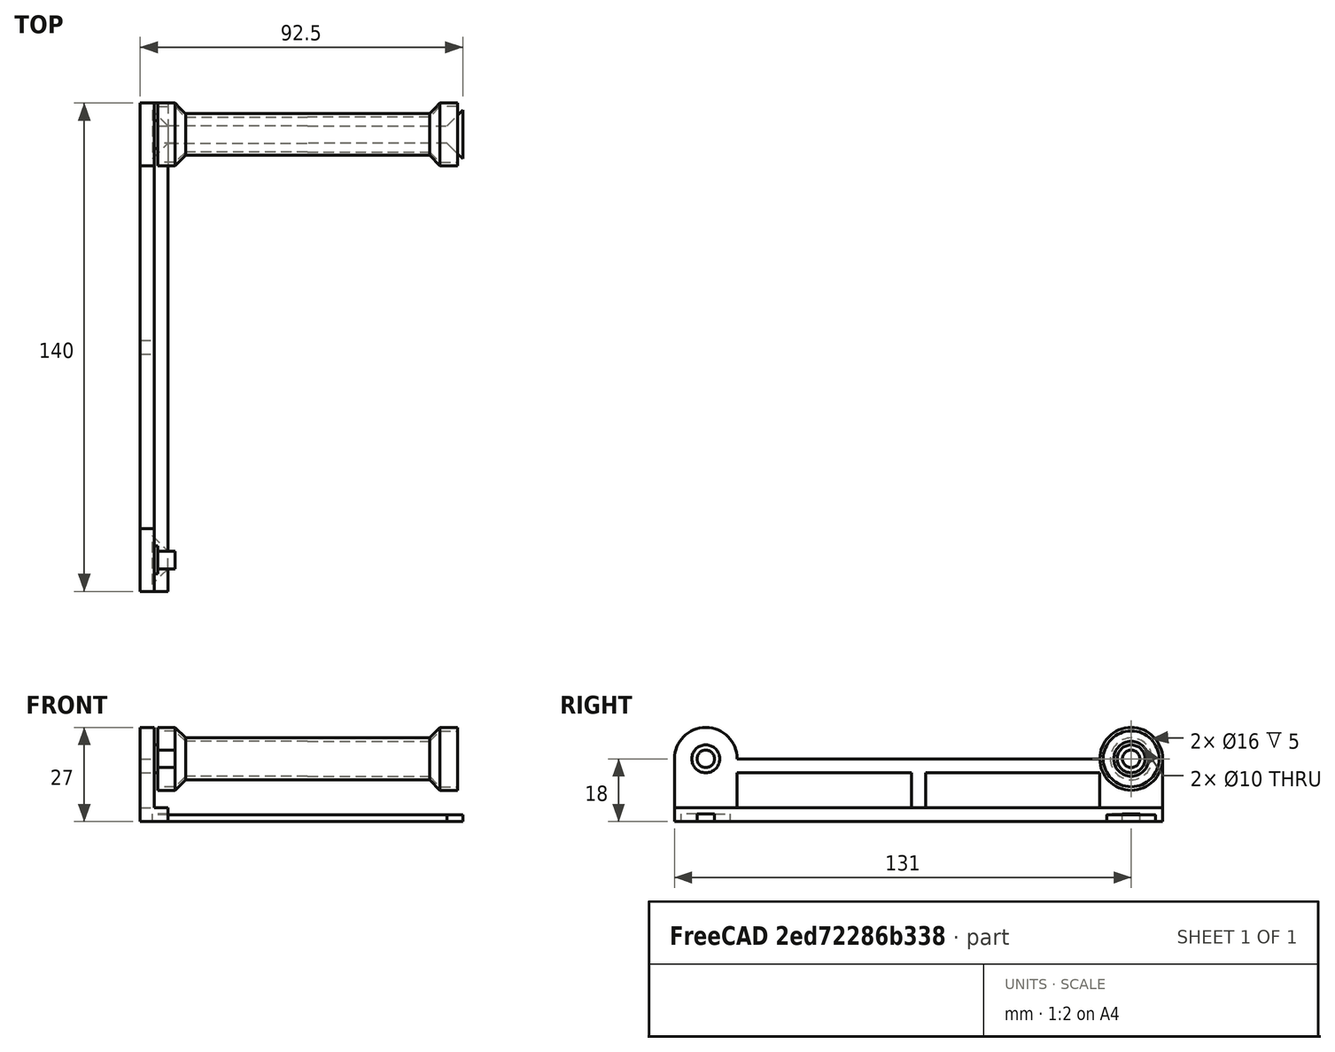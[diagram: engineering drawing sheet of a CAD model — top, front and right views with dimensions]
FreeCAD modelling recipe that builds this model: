
FCSTD DOCUMENT  (FreeCAD 0.21R33771 (Git))
Label: FilamentRoller
License: All rights reserved
LicenseURL: http://en.wikipedia.org/wiki/All_rights_reserved
objects: Sketcher::SketchObject×7, PartDesign::Pad×7, PartDesign::Mirrored×3, PartDesign::Body×3, Mesh::Feature×3, PartDesign::AdditiveLoft×1, PartDesign::SubShapeBinder×1, PartDesign::Pocket×1
note: 32 computed .brp shape members not serialized (recipe doc carries the construction recipe); baked Part::Feature solids carry a one-line shape summary decoded from their .brp

FEATURE [Sketcher::SketchObject] Sketch  label="FloorSketch"
  FullyConstrained = true
  MapMode = 5
  Support = -> [XY_Plane]
  sketch-geometry (4):
    g0: LineSegment StartX=-48 StartY=70 StartZ=0 EndX=-40 EndY=70 EndZ=0
    g1: LineSegment StartX=-40 StartY=70 StartZ=0 EndX=-40 EndY=0 EndZ=0
    g2: LineSegment StartX=-40 StartY=0 StartZ=0 EndX=-48 EndY=0 EndZ=0
    g3: LineSegment StartX=-48 StartY=0 StartZ=0 EndX=-48 EndY=70 EndZ=0
  constraints (12):
    c: Coincident(g0,g1)
    c: Coincident(g1,g2)
    c: Coincident(g2,g3)
    c: Coincident(g3,g0)
    c: Horizontal(g0)
    c: Horizontal(g2)
    c: Vertical(g1)
    c: DistanceX(g0,g0) = 8
    c: DistanceX(g0,g-1) = 48
    c: DistanceY(g-1,g0) = 70
    c: PointOnObject(g2,g-1)
    c: Vertical(g3)
FEATURE [PartDesign::Pad] Pad  label="FloorPad"
  Direction = (0,0,1)
  Length = 4
  Length2 = 10
  Profile = -> Sketch
  ReferenceAxis = -> Sketch [N_Axis]
  Type = 0
FEATURE [Sketcher::SketchObject] Sketch001  label="BearingBackingSketch"
  ExternalGeometry = -> [Pad]
  FullyConstrained = true
  MapMode = 5
  Placement = pos=(-48,0,0) rot=(0.57735,-0.57735,-0.57735;2.0944rad)
  Support = -> [Pad]
  sketch-geometry (12):
    g0: ArcOfCircle CenterX=-61 CenterY=18 CenterZ=0 NormalX=0 NormalY=0 NormalZ=1 AngleXU=0 Radius=9 StartAngle=0 EndAngle=3.14159
    g1: GeomPoint X=-70 Y=18 Z=0
    g2: LineSegment StartX=-70 StartY=4 StartZ=0 EndX=-70 EndY=18 EndZ=0
    g3: LineSegment StartX=-70 StartY=4 StartZ=0 EndX=-52 EndY=4 EndZ=0
    g4: LineSegment StartX=-52 StartY=14 StartZ=0 EndX=-52 EndY=4 EndZ=0
    g5: GeomPoint X=0 Y=18 Z=0
    g6: GeomPoint X=0 Y=4 Z=0
    g7: LineSegment StartX=-52 StartY=18 StartZ=0 EndX=0 EndY=18 EndZ=0
    g8: LineSegment StartX=0 StartY=18 StartZ=0 EndX=0 EndY=4 EndZ=0
    g9: LineSegment StartX=0 StartY=4 StartZ=0 EndX=-2 EndY=4 EndZ=0
    g10: LineSegment StartX=-2 StartY=4 StartZ=0 EndX=-2 EndY=14 EndZ=0
    g11: LineSegment StartX=-2 StartY=14 StartZ=0 EndX=-52 EndY=14 EndZ=0
  constraints (30):
    c: Diameter(g0) = 18  'bearingDiameter'
    c: Vertical(g1,g-5)
    c: Coincident(g2,g-6)
    c: Coincident(g2,g1)
    c: PointOnObject(g4,g-6)
    c: Coincident(g0,g2)
    c: Coincident(g3,g2)
    c: Coincident(g3,g4)
    c: Vertical(g4)
    c: PointOnObject(g5,g-2)
    c: PointOnObject(g6,g-2)
    c: Coincident(g7,g0)
    c: Coincident(g7,g5)
    c: Coincident(g9,g6)
    c: Coincident(g11,g4)
    c: Horizontal(g7)
    c: Vertical(g4,g0)
    c: DistanceY(g4,g0) = 4
    c: Coincident(g8,g7)
    c: Coincident(g8,g9)
    c: Coincident(g9,g10)
    c: Coincident(g10,g11)
    c: PointOnObject(g9,g-6)
    c: PointOnObject(g8,g-6)
    c: Vertical(g10)
    c: DistanceX(g10,g7) = 2
    c: Horizontal(g11)
    c: Horizontal(g0,g0)
    c: Horizontal(g0,g0)
    c: DistanceY(g0) = 18
FEATURE [PartDesign::Pad] Pad001  label="BearingBackingPad"
  BaseFeature = -> Pad
  Direction = (-1,0,0)
  Length = 4
  Length2 = 10
  Profile = -> Sketch001
  ReferenceAxis = -> Sketch001 [N_Axis]
  Reversed = true
  Type = 0
FEATURE [Sketcher::SketchObject] Sketch002  label="BearingPinSketch"
  ExternalGeometry = -> [Pad001]
  FullyConstrained = true
  MapMode = 5
  Placement = pos=(-44,0,0) rot=(0.57735,0.57735,0.57735;2.0944rad)
  Support = -> [Pad001]
  sketch-geometry (1):
    g0: Circle CenterX=61 CenterY=18 CenterZ=0 NormalX=0 NormalY=0 NormalZ=1 AngleXU=0 Radius=2.5
  constraints (2):
    c: Diameter(g0) = 5
    c: Coincident(g0,g-3)
FEATURE [PartDesign::Pad] Pad002  label="BearingPinPad"
  BaseFeature = -> Pad001
  Direction = (1,0,0)
  Length = 6
  Length2 = 10
  Profile = -> Sketch002
  ReferenceAxis = -> Sketch002 [N_Axis]
  Type = 0
FEATURE [Sketcher::SketchObject] Sketch003
  AttachmentOffset = pos=(0,0,-43) rot=(0,0,1;0rad)
  FullyConstrained = true
  MapMode = 5
  Placement = pos=(-43,9.5e-15,-9.5e-15) rot=(0.57735,0.57735,0.57735;2.0944rad)
  Support = -> [YZ_Plane001]
  sketch-geometry (2):
    g0: Circle CenterX=61 CenterY=18 CenterZ=0 NormalX=0 NormalY=0 NormalZ=1 AngleXU=0 Radius=8
    g1: Circle CenterX=61 CenterY=18 CenterZ=0 NormalX=0 NormalY=0 NormalZ=1 AngleXU=0 Radius=9
  constraints (5):
    c: Diameter(g0) = 16
    c: Coincident(g1,g0)
    c: Diameter(g1) = 18
    c: DistanceY(g-1,g0) = 18
    c: DistanceX(g-1,g0) = 61
FEATURE [PartDesign::Pad] Pad003
  Direction = (1,-2e-16,3e-16)
  Length = 5
  Length2 = 10
  Placement = pos=(0,0,0) rot=(0.57735,0.57735,0.57735;2.0944rad)
  Profile = -> Sketch003
  ReferenceAxis = -> Sketch003 [N_Axis]
  Type = 0
FEATURE [Sketcher::SketchObject] Sketch004
  AttachmentOffset = pos=(0,0,-35) rot=(0,0,1;0rad)
  ExternalGeometry = -> [Pad003]
  FullyConstrained = true
  MapMode = 5
  Placement = pos=(-35,7.8e-15,-7.8e-15) rot=(0.57735,0.57735,0.57735;2.0944rad)
  Support = -> [YZ_Plane001]
  sketch-geometry (2):
    g0: Circle CenterX=61 CenterY=18 CenterZ=0 NormalX=0 NormalY=0 NormalZ=1 AngleXU=0 Radius=6
    g1: Circle CenterX=61 CenterY=18 CenterZ=0 NormalX=0 NormalY=0 NormalZ=1 AngleXU=0 Radius=5
  constraints (4):
    c: Coincident(g0,g-3)
    c: Coincident(g1,g0)
    c: Diameter(g0) = 12
    c: Diameter(g1) = 10
FEATURE [PartDesign::AdditiveLoft] AdditiveLoft
  BaseFeature = -> Pad003
  Closed = false
  Placement = pos=(0,0,0) rot=(0.57735,0.57735,0.57735;2.0944rad)
  Profile = -> Pad003 [Face4]
  Ruled = false
  Sections = -> [Sketch004]
FEATURE [PartDesign::Pad] Pad004
  BaseFeature = -> AdditiveLoft
  Direction = (1,-4e-16,8e-16)
  Length = 35
  Length2 = 10
  Placement = pos=(0,0,0) rot=(0.57735,0.57735,0.57735;2.0944rad)
  Profile = -> AdditiveLoft [Face5]
  Type = 0
FEATURE [PartDesign::Mirrored] Mirrored001
  BaseFeature = -> Pad004
  MirrorPlane = -> YZ_Plane001
  Originals = -> [Pad003,AdditiveLoft,Pad004]
  Placement = pos=(0,0,0) rot=(0.57735,0.57735,0.57735;2.0944rad)
FEATURE [PartDesign::Body] Body001  label="Roller"
  Group = -> [Sketch003,Pad003,Sketch004,AdditiveLoft,Pad004,Mirrored001]
  Origin = -> Origin001
  Tip = -> Mirrored001
FEATURE [Sketcher::SketchObject] Sketch005  label="BearingStandoffSketch"
  ExternalGeometry = -> [Pad002]
  FullyConstrained = true
  MapMode = 5
  Placement = pos=(-44,0,0) rot=(0.57735,0.57735,0.57735;2.0944rad)
  Support = -> [Pad002]
  sketch-geometry (1):
    g0: Circle CenterX=61 CenterY=18 CenterZ=0 NormalX=0 NormalY=0 NormalZ=1 AngleXU=0 Radius=4
  constraints (2):
    c: Diameter(g0) = 8
    c: Coincident(g0,g-3)
FEATURE [PartDesign::Pad] Pad005  label="BearingStandoffPadding"
  BaseFeature = -> Pad002
  Direction = (1,0,0)
  Length = 1
  Length2 = 10
  Profile = -> Sketch005
  ReferenceAxis = -> Sketch005 [N_Axis]
  Type = 0
FEATURE [Sketcher::SketchObject] Sketch007  label="BinderBaseSketch"
  FullyConstrained = true
  MapMode = 5
  Support = -> [XY_Plane002]
  sketch-geometry (6):
    g0: LineSegment StartX=-44.5 StartY=68 StartZ=0 EndX=-44.5 EndY=54 EndZ=0
    g1: LineSegment StartX=-44.5 StartY=54 StartZ=0 EndX=-40 EndY=58.5 EndZ=0
    g2: LineSegment StartX=-40 StartY=58.5 StartZ=0 EndX=0 EndY=58.5 EndZ=0
    g3: LineSegment StartX=0 StartY=58.5 StartZ=0 EndX=0 EndY=63.5 EndZ=0
    g4: LineSegment StartX=0 StartY=63.5 StartZ=0 EndX=-40 EndY=63.5 EndZ=0
    g5: LineSegment StartX=-40 StartY=63.5 StartZ=0 EndX=-44.5 EndY=68 EndZ=0
  constraints (18):
    c: Vertical(g0)
    c: Coincident(g0,g1)
    c: PointOnObject(g2,g-2)
    c: Horizontal(g2)
    c: Coincident(g2,g3)
    c: PointOnObject(g3,g-2)
    c: Coincident(g3,g4)
    c: Horizontal(g4)
    c: Coincident(g4,g5)
    c: Coincident(g5,g0)
    c: Coincident(g1,g2)
    c: Angle(g1,g0) = 0.785398
    c: Angle(g0,g5) = 0.785398
    c: Vertical(g4,g1)
    c: DistanceY(g0,g0) = 14
    c: DistanceY(g3,g3) = 5
    c: DistanceX(g4,g4) = 40
    c: DistanceY(g-1,g2) = 58.5
FEATURE [PartDesign::Pad] Pad006  label="BinderBasePad"
  Direction = (0,0,1)
  Length = 2
  Length2 = 10
  Profile = -> Sketch007
  ReferenceAxis = -> Sketch007 [N_Axis]
  Type = 0
FEATURE [PartDesign::Mirrored] Mirrored002  label="BinderMirror"
  BaseFeature = -> Pad006
  MirrorPlane = -> Sketch007 [V_Axis]
  Originals = -> [Pad006]
FEATURE [PartDesign::Body] Body002  label="Binder"
  Group = -> [Sketch007,Pad006,Mirrored002]
  Origin = -> Origin002
  Tip = -> Mirrored002
FEATURE [PartDesign::SubShapeBinder] Binder  label="BinderBaseBinder"
  BindCopyOnChange = 0
  BindMode = 0
  ClaimChildren = false
  Context = -> Body [Binder.]
  Fuse = false
  MakeFace = true
  OffsetFill = false
  OffsetIntersection = false
  OffsetJoinType = 2
  OffsetOpenResult = false
  PartialLoad = false
  Relative = true
  Support = -> [Body002[Pad006.Sketch007.]]
  _Version = 2
FEATURE [PartDesign::Pocket] Pocket
  BaseFeature = -> Pad005
  Direction = (0,0,-1)
  Length = 2.2
  Length2 = 5
  Profile = -> Binder
  Reversed = true
  Type = 0
FEATURE [Mesh::Feature] Mesh001  label="Roller (Meshed)"
FEATURE [Mesh::Feature] Mesh002  label="Binder (Meshed)"
FEATURE [PartDesign::Mirrored] Mirrored
  BaseFeature = -> Pocket
  MirrorPlane = -> XZ_Plane
  Originals = -> [Pad,Pad001,Pad002,Pad005,Pocket]
FEATURE [PartDesign::Body] Body  label="SideRail"
  Group = -> [Sketch,Pad,Sketch001,Pad001,Sketch002,Pad002,Sketch005,Pad005,Binder,Pocket,Mirrored]
  Origin = -> Origin
  Tip = -> Mirrored
FEATURE [Mesh::Feature] Mesh  label="SideRail (Meshed)"
